# Revit family: Basin-Wall_Mounted-American_Standard-Declyn_0321_Series
name_source: partatom
category: Plumbing Fixtures
units: mm (PartAtom-declared; Revit-internal decimal feet)

## family parameters
Cut with Voids When Loaded = No
Host = Face
OmniClass Number = 23.45.05.14.14
OmniClass Title = Sinks/Lavatories
Part Type = Normal
Room Calculation Point = No
Round Connector Dimension = Use Diameter
Shared = Yes

## types (2) — shared parameters
Assembly Code = D2010310
Bowl Shape = Rectangular
CW Connection = Yes
CWFU = 1.5
Cold Water Connection Diameter = 1/2"
Cold Water Connection Height = 9 1/4"
Cold Water Connection Radius = 1/4"
Cold Water Connection Width = 4"
Default Elavation Constraint = 31"
Default Elevation = 31"
Finish = Vitreous China-American Standard-020-White
HW Connection = Yes
HWFU = 1.5
Hanger Height = 6 1/2"
Height = 7 3/4"
Hot Water Connection Diameter = 0"
Hot Water Connection Height = 9 1/4"
Hot Water Connection Radius = 1/4"
Hot Water Connection Width = 4"
IAPMO Compliance = Compliance Certifications Meets or Exceeds the Following Specifications:  ASME A112.19.2/CSA 45.1
Installation Type = Wall mounted
Length = 17"
Manufacturer = American Standard
Material = Vitreous China-American Standard-020-White
Product Documentation Link = https://americanstandard.box.com
Product Page URL = https://www.americanstandard.ca
Revised Date = 08/09/2022
URL = http://www.americanstandard.ca
Vent Connection = No
WFU = 2
Waste Connection = Yes
Waste Connection Diameter = 1 1/4"
Waste Connection Height = 13 1/2"
Waste Connection Radius = 3/4"
Width = 19"

## per-type parameters (varying)
| type | Concealed Arms Support | Description | Wall Hanger |
| 0321026.020 | No | Declyn™ Wall-Hung Sink With 4-Inch Centerset, Wall Hanger Included | Yes |
| 0321075.020 | Yes | Declyn™ Wall-Hung Sink With 4-Inch Centerset, for Concealed Arms | No |

note: column(s) folded — value = type name in every type: Model

## geometry (parser evidence)
native form markers: Sweep x2
no freeform markers — native parametric forms only
